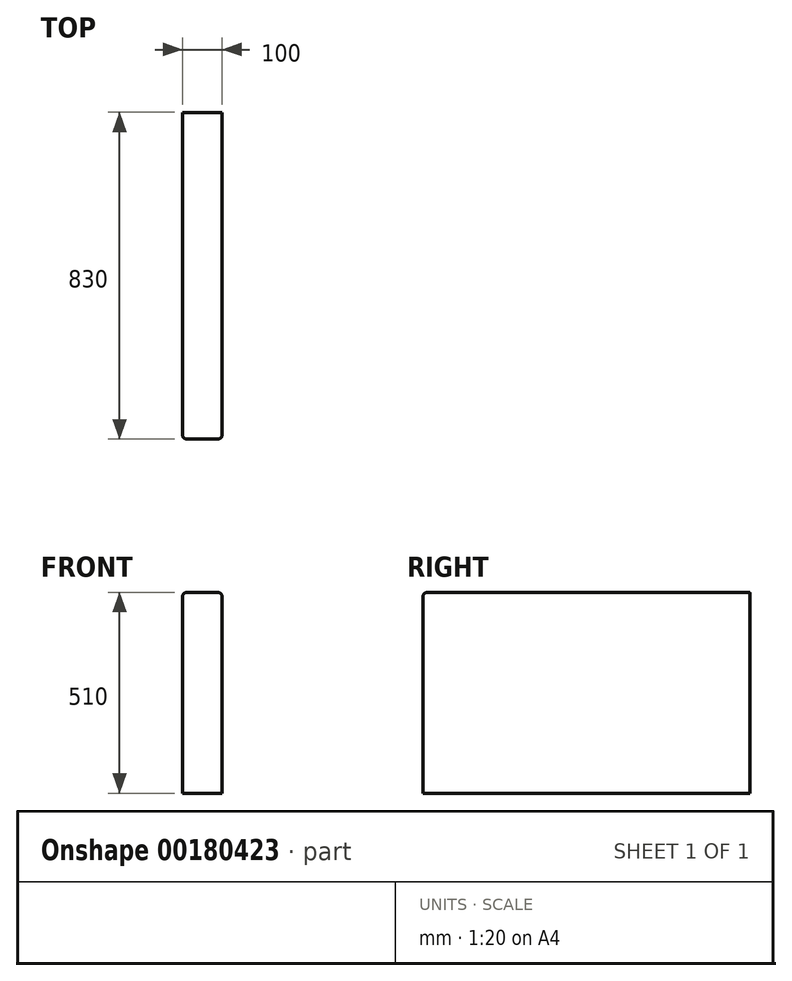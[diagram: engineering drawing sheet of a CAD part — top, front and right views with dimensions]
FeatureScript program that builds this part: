
annotation { "Feature Type Name" : "Feature", "Feature Type Description" : "" }
export const myFeature = defineFeature(function(context is Context, id is Id, definition is map)
    precondition{}
    {
        {
            var Q0;
            Q0=qCreatedBy(makeId("Top.planeOp"),FACE);
            var sketch = newSketch(context, id + "F0", { "sketchPlane" : qUnion([Q0])});
            skLineSegment(sketch, "E0.bottom", {"start": v(-63.94, -380.86) * mm, "end": v(36.06, -380.86) * mm});
            skLineSegment(sketch, "E0.top", {"start": v(-63.94, 449.14) * mm, "end": v(36.06, 449.14) * mm});
            skLineSegment(sketch, "E0.left", {"start": v(-63.94, -380.86) * mm, "end": v(-63.94, 449.14) * mm});
            skLineSegment(sketch, "E0.right", {"start": v(36.06, -380.86) * mm, "end": v(36.06, 449.14) * mm});
            skSolve(sketch);
        }
        {
            var Q0;
            Q0 = qSketchRegion(id + "F0", true);
            extrude(context, id + "F1", {"entities" : qUnion([Q0]), "depth" : 510 * mm});
        }
        {
            var Q0;
            Q0=makeQuery(id+"F1.opExtrude","CAP_EDGE",EDGE,{"disambiguationData":[OSD([sQuery(id+"F0.wireOp",EDGE,"E0.right")])],"isStart":false});
            var Q1;
            Q1=makeQuery(id+"F1.opExtrude","CAP_EDGE",EDGE,{"disambiguationData":[OSD([sQuery(id+"F0.wireOp",EDGE,"E0.left")])],"isStart":false});
            var Q2;
            Q2=makeQuery(id+"F1.opExtrude","CAP_EDGE",EDGE,{"disambiguationData":[OSD([sQuery(id+"F0.wireOp",EDGE,"E0.bottom")])],"isStart":false});
            var Q3;
            Q3=makeQuery(id+"F1.opExtrude","SWEPT_EDGE",EDGE,{"disambiguationData":[OSD([sQuery(id+"F0.wireOp",EDGE,"E0.bottom"),sQuery(id+"F0.wireOp",EDGE,"E0.right")])]});
            var Q4;
            Q4=makeQuery(id+"F1.opExtrude","SWEPT_EDGE",EDGE,{"disambiguationData":[OSD([sQuery(id+"F0.wireOp",EDGE,"E0.bottom"),sQuery(id+"F0.wireOp",EDGE,"E0.left")])]});
            fillet(context, id + "F2", {"entities" : qUnion([Q0, Q1, Q2, Q3, Q4]), "radius" : 10 * mm, "tangentPropagation" : true, "allowEdgeOverflow" : false});
        }
    });
